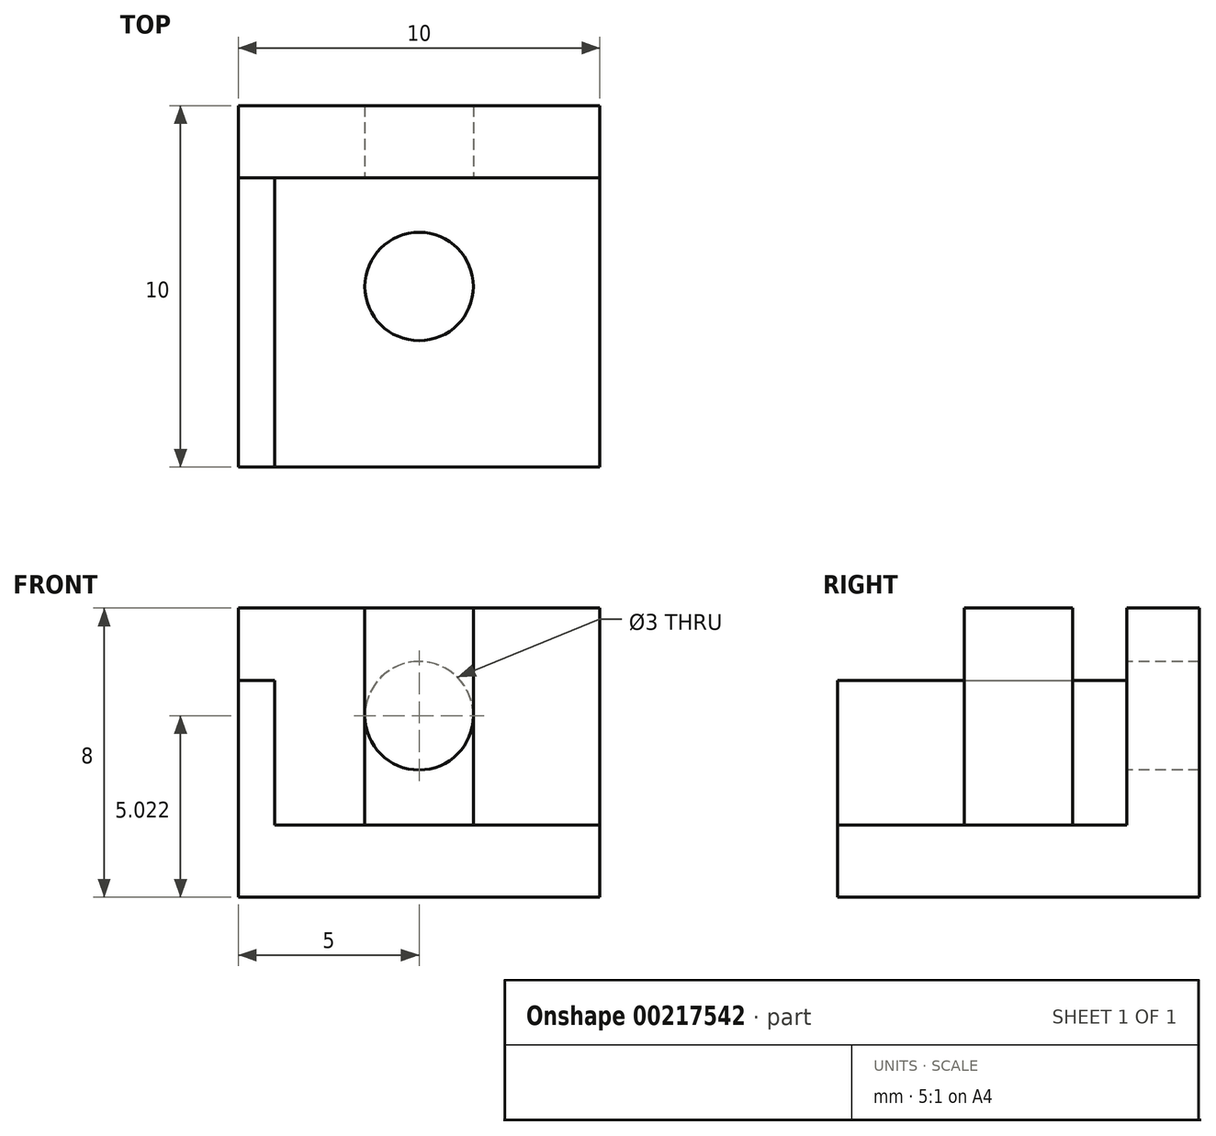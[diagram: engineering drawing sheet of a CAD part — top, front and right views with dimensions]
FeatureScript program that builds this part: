
annotation { "Feature Type Name" : "Feature", "Feature Type Description" : "" }
export const myFeature = defineFeature(function(context is Context, id is Id, definition is map)
    precondition{}
    {
        {
            var Q0;
            Q0=qCreatedBy(makeId("Top.planeOp"),FACE);
            var sketch = newSketch(context, id + "F0", { "sketchPlane" : qUnion([Q0])});
            skLineSegment(sketch, "E0.bottom", {"start": v(-5, -5) * mm, "end": v(5, -5) * mm});
            skLineSegment(sketch, "E0.top", {"start": v(-5, 5) * mm, "end": v(5, 5) * mm});
            skLineSegment(sketch, "E0.left", {"start": v(-5, -5) * mm, "end": v(-5, 5) * mm});
            skLineSegment(sketch, "E0.right", {"start": v(5, -5) * mm, "end": v(5, 5) * mm});
            skPoint(sketch, "E0.middle", {"position": v(0, 0) * mm});
            skSolve(sketch);
        }
        {
            var Q0;
            Q0=qSketchRegion(id+"F0",true);
            extrude(context, id + "F1", {"entities" : qUnion([Q0]), "depth" : 2 * mm});
        }
        {
            var Q0;
            Q0=makeQuery(id+"F1.opExtrude","CAP_FACE",FACE,{"disambiguationData":[OSD([sQuery(id+"F0.wireOp",EDGE,"E0.bottom"),sQuery(id+"F0.wireOp",EDGE,"E0.top"),sQuery(id+"F0.wireOp",EDGE,"E0.left"),sQuery(id+"F0.wireOp",EDGE,"E0.right")])],"isStart":false});
            var sketch = newSketch(context, id + "F2", { "sketchPlane" : qUnion([Q0])});
            skLineSegment(sketch, "E1.bottom", {"start": v(-5, 5) * mm, "end": v(5, 5) * mm});
            skLineSegment(sketch, "E1.top", {"start": v(-5, 3) * mm, "end": v(5, 3) * mm});
            skLineSegment(sketch, "E1.left", {"start": v(-5, 5) * mm, "end": v(-5, 3) * mm});
            skLineSegment(sketch, "E1.right", {"start": v(5, 5) * mm, "end": v(5, 3) * mm});
            skSolve(sketch);
        }
        {
            var Q0;
            Q0=qSketchRegion(id+"F2",true);
            extrude(context, id + "F3", {"entities" : qUnion([Q0]), "operationType" : NewBodyOperationType.ADD, "depth" : 6 * mm});
        }
        {
            var Q0;
            Q0=makeQuery(id+"F3.opExtrude","SWEPT_FACE",FACE,{"disambiguationData":[OSD([sQuery(id+"F2.wireOp",EDGE,"E1.top")])]});
            var sketch = newSketch(context, id + "F4", { "sketchPlane" : qUnion([Q0])});
            skCircle(sketch, "E2", {"center": v(0, 5.02) * mm, "radius": 1.5 * mm});
            skSolve(sketch);
        }
        {
            var Q0;
            Q0=makeQuery(id+"F4.imprint","IMPRINT",FACE,{"disambiguationData":[TD([[makeQuery(id+"F4.imprint","IMPRINT",EDGE,{"derivedFrom":sQuery(id+"F4.wireOp",EDGE,"E2")}),1.0]])]});
            extrude(context, id + "F5", {"entities" : qUnion([Q0]), "operationType" : NewBodyOperationType.REMOVE, "oppositeDirection" : true, "depth" : 25 * mm});
        }
        {
            var Q0;
            Q0=makeQuery(id+"F1.opExtrude","CAP_FACE",FACE,{"disambiguationData":[OSD([sQuery(id+"F0.wireOp",EDGE,"E0.bottom"),sQuery(id+"F0.wireOp",EDGE,"E0.top"),sQuery(id+"F0.wireOp",EDGE,"E0.left"),sQuery(id+"F0.wireOp",EDGE,"E0.right")])],"isStart":false});
            var sketch = newSketch(context, id + "F6", { "sketchPlane" : qUnion([Q0])});
            skCircle(sketch, "E3", {"center": v(0, 0) * mm, "radius": 1.5 * mm});
            skSolve(sketch);
        }
        {
            var Q0;
            Q0=makeQuery(id+"F6.imprint","IMPRINT",FACE,{"disambiguationData":[TD([[makeQuery(id+"F6.imprint","IMPRINT",EDGE,{"derivedFrom":sQuery(id+"F6.wireOp",EDGE,"E3")}),1.0]])]});
            extrude(context, id + "F7", {"entities" : qUnion([Q0]), "operationType" : NewBodyOperationType.ADD, "depth" : 6 * mm});
        }
        {
            var Q0;
            Q0=makeQuery(id+"F1.opExtrude","CAP_FACE",FACE,{"disambiguationData":[OSD([sQuery(id+"F0.wireOp",EDGE,"E0.bottom"),sQuery(id+"F0.wireOp",EDGE,"E0.top"),sQuery(id+"F0.wireOp",EDGE,"E0.left"),sQuery(id+"F0.wireOp",EDGE,"E0.right")])],"isStart":false});
            var sketch = newSketch(context, id + "F8", { "sketchPlane" : qUnion([Q0])});
            skLineSegment(sketch, "E4.bottom", {"start": v(-5, -5) * mm, "end": v(-4, -5) * mm});
            skLineSegment(sketch, "E4.top", {"start": v(-5, 3) * mm, "end": v(-4, 3) * mm});
            skLineSegment(sketch, "E4.left", {"start": v(-5, -5) * mm, "end": v(-5, 3) * mm});
            skLineSegment(sketch, "E4.right", {"start": v(-4, -5) * mm, "end": v(-4, 3) * mm});
            skSolve(sketch);
        }
        {
            var Q0;
            Q0=makeQuery(id+"F8.imprint","IMPRINT",FACE,{"disambiguationData":[TD([[makeQuery(id+"F8.imprint","IMPRINT",EDGE,{"derivedFrom":sQuery(id+"F8.wireOp",EDGE,"E4.bottom")}),1.0]])]});
            extrude(context, id + "F9", {"entities" : qUnion([Q0]), "operationType" : NewBodyOperationType.ADD, "depth" : 4 * mm});
        }
    });
